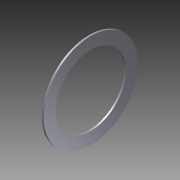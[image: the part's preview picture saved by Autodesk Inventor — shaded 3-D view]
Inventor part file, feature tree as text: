
AUTODESK INVENTOR PART (.ipt)
format: ipt  version: 2013 SP2 (Build 170200200, 200)  size: 90,624 bytes
history: native  units: mm
features: other x7, revolve x1, sketch x1
ambient origin geometry x8: Origin, YZ Plane, XZ Plane, XY Plane, X Axis, Y Axis, Z Axis, Center Point
bodies: Solid1 (feature_tree)
feature tree (9):
  revolve  "Revolution1"  [1 undecoded]
  other  "ring_XY"
  other  "ring_YZ"
  other  "ring_ZX"
  other  "ring_X"
  other  "ring_Y"
  other  "ring_Z"
  other  "ring_Center"
  sketch  "Sketch_1"  dims[d0=360.0deg]
note: 1 required parameter value undecoded (feature->parameter linkage not recoverable at this tier; creation-order binding heuristic only, values carry confidence <= 0.55)
